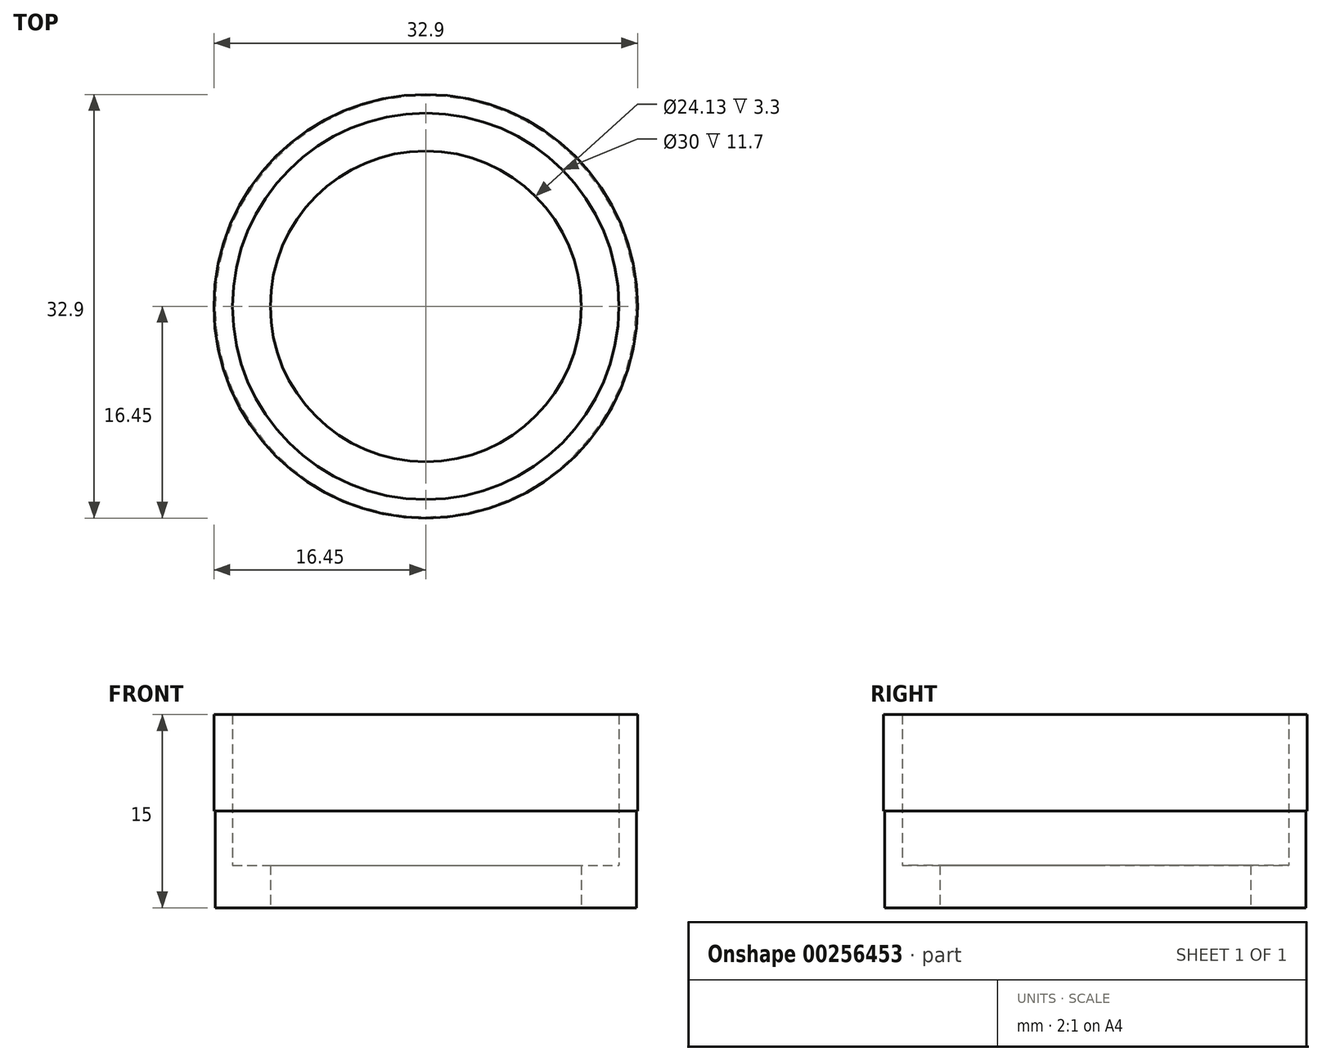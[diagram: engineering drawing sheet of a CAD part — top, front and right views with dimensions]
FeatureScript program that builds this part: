
annotation { "Feature Type Name" : "Feature", "Feature Type Description" : "" }
export const myFeature = defineFeature(function(context is Context, id is Id, definition is map)
    precondition{}
    {
        {
            var Q0;
            Q0=qCreatedBy(makeId("Front.planeOp"),FACE);
            var sketch = newSketch(context, id + "F0", { "sketchPlane" : qUnion([Q0])});
            skLineSegment(sketch, "E0", {"start": v(4.02, 0) * mm, "end": v(5.45, 0) * mm});
            skLineSegment(sketch, "E1", {"start": v(5.45, 0) * mm, "end": v(5.45, 2.5) * mm});
            skLineSegment(sketch, "E2", {"start": v(5.45, 2.5) * mm, "end": v(5.48, 2.5) * mm});
            skLineSegment(sketch, "E3", {"start": v(5.48, 2.5) * mm, "end": v(5.48, 5) * mm});
            skLineSegment(sketch, "E4", {"start": v(5.48, 5) * mm, "end": v(5, 5) * mm});
            skLineSegment(sketch, "E5", {"start": v(5, 5) * mm, "end": v(5, 1.1) * mm});
            skLineSegment(sketch, "E6", {"start": v(5, 1.1) * mm, "end": v(4.02, 1.1) * mm});
            skLineSegment(sketch, "E7", {"start": v(4.02, 1.1) * mm, "end": v(4.02, 0) * mm});
            skLineSegment(sketch, "E8", {"start": v(0, 0) * mm, "end": v(0, 5) * mm, "construction": true});
            skSolve(sketch);
        }
        {
            var Q0;
            Q0=makeQuery(id+"F0.imprint","IMPRINT",FACE,{"disambiguationData":[TD([[makeQuery(id+"F0.imprint","IMPRINT",EDGE,{"derivedFrom":sQuery(id+"F0.wireOp",EDGE,"E0")}),1.0]])]});
            var Q1;
            Q1=sQuery(id+"F0.wireOp",EDGE,"E8");
            revolve(context, id + "F1", {"entities" : qUnion([Q0]), "axis" : qUnion([Q1]), "revolveType" : RevolveType.FULL});
        }
        {
            var Q0;
            Q0=makeQuery(id+"F1.opRevolve","SWEPT_BODY",BODY,{"disambiguationData":[OSD([sQuery(id+"F0.wireOp",EDGE,"E0"),sQuery(id+"F0.wireOp",EDGE,"E1"),sQuery(id+"F0.wireOp",EDGE,"E2"),sQuery(id+"F0.wireOp",EDGE,"E3"),sQuery(id+"F0.wireOp",EDGE,"E4"),sQuery(id+"F0.wireOp",EDGE,"E5"),sQuery(id+"F0.wireOp",EDGE,"E6"),sQuery(id+"F0.wireOp",EDGE,"E7")])]});
            var Q1;
            Q1=qCreatedBy(makeId("Origin.pointOp"),VERTEX);
            transform(context, id + "F2", {"entities" : qUnion([Q0]), "transformType" : TransformType.SCALE_UNIFORMLY, "scale" : 3, "makeCopy" : false, "scalePoint" : qUnion([Q1])});
        }
    });
